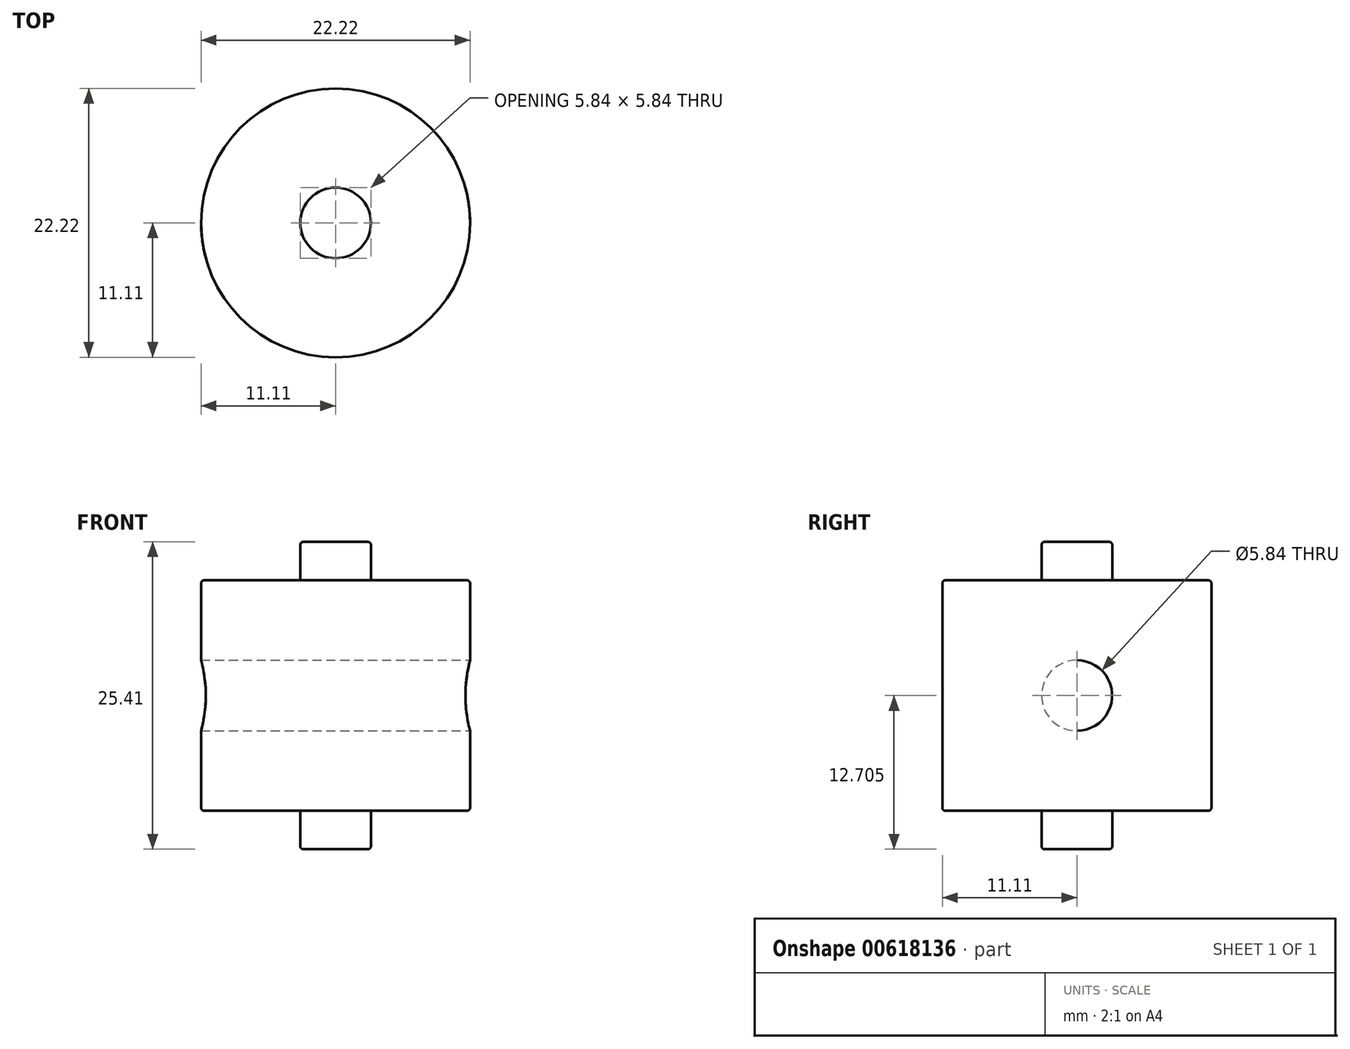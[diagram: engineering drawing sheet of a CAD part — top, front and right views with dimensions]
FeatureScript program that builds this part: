
annotation { "Feature Type Name" : "Feature", "Feature Type Description" : "" }
export const myFeature = defineFeature(function(context is Context, id is Id, definition is map)
    precondition{}
    {
        {
            var Q0;
            Q0=qCreatedBy(makeId("Top.planeOp"),FACE);
            var sketch = newSketch(context, id + "F0", { "sketchPlane" : qUnion([Q0])});
            skCircle(sketch, "E0", {"center": v(0, 0) * mm, "radius": 11.11 * mm});
            skCircle(sketch, "E1", {"center": v(0, 0) * mm, "radius": 2.92 * mm});
            skSolve(sketch);
        }
        {
            var Q0;
            Q0 = qSketchRegion(id + "F0", true);
            extrude(context, id + "F1", {"entities" : qUnion([Q0]), "depth" : 19.05 * mm, "offsetDistance" : 25.4 * mm});
        }
        {
            var Q0;
            Q0=qCreatedBy(makeId("Top.planeOp"),FACE);
            var sketch = newSketch(context, id + "F2", { "sketchPlane" : qUnion([Q0])});
            skCircle(sketch, "E2", {"center": v(0, 0) * mm, "radius": 2.92 * mm});
            skSolve(sketch);
        }
        {
            var Q0;
            Q0 = qSketchRegion(id + "F2", true);
            extrude(context, id + "F3", {"entities" : qUnion([Q0]), "operationType" : NewBodyOperationType.ADD, "depth" : 22.22 * mm, "offsetDistance" : 25.4 * mm, "hasSecondDirection" : true, "secondDirectionOppositeDirection" : true, "secondDirectionDepth" : 3.17 * mm});
        }
        {
            var Q0;
            Q0=qCreatedBy(makeId("Right.planeOp"),FACE);
            var sketch = newSketch(context, id + "F4", { "sketchPlane" : qUnion([Q0])});
            skCircle(sketch, "E3", {"center": v(0, 9.53) * mm, "radius": 2.92 * mm});
            skSolve(sketch);
        }
        {
            var Q0;
            Q0 = qSketchRegion(id + "F4", true);
            extrude(context, id + "F5", {"entities" : qUnion([Q0]), "operationType" : NewBodyOperationType.REMOVE, "endBound" : BoundingType.SYMMETRIC, "oppositeDirection" : true, "depth" : 25.4 * mm, "offsetDistance" : 25.4 * mm});
        }
        {
            var Q0;
            Q0=makeQuery(id+"F3.opExtrude","CAP_EDGE",EDGE,{"disambiguationData":[OSD([sQuery(id+"F2.wireOp",EDGE,"E2")])],"isStart":false});
            fillet(context, id + "F6", {"entities" : qUnion([Q0]), "radius" : 0.25 * mm, "tangentPropagation" : true, "allowEdgeOverflow" : false});
        }
        {
            var Q0;
            Q0=makeQuery(id+"F3.opExtrude","CAP_EDGE",EDGE,{"disambiguationData":[OSD([sQuery(id+"F2.wireOp",EDGE,"E2")])],"isStart":true});
            fillet(context, id + "F7", {"entities" : qUnion([Q0]), "radius" : 0.25 * mm, "tangentPropagation" : true, "allowEdgeOverflow" : false});
        }
        {
            var Q0;
            Q0=makeQuery(id+"F1.opExtrude","CAP_EDGE",EDGE,{"disambiguationData":[OSD([sQuery(id+"F0.wireOp",EDGE,"E0")])],"isStart":true});
            fillet(context, id + "F8", {"entities" : qUnion([Q0]), "radius" : 0.25 * mm, "tangentPropagation" : true, "allowEdgeOverflow" : false});
        }
        {
            var Q0;
            Q0=makeQuery(id+"F1.opExtrude","CAP_EDGE",EDGE,{"disambiguationData":[OSD([sQuery(id+"F0.wireOp",EDGE,"E0")])],"isStart":false});
            fillet(context, id + "F9", {"entities" : qUnion([Q0]), "radius" : 0.25 * mm, "tangentPropagation" : true, "allowEdgeOverflow" : false});
        }
    });
